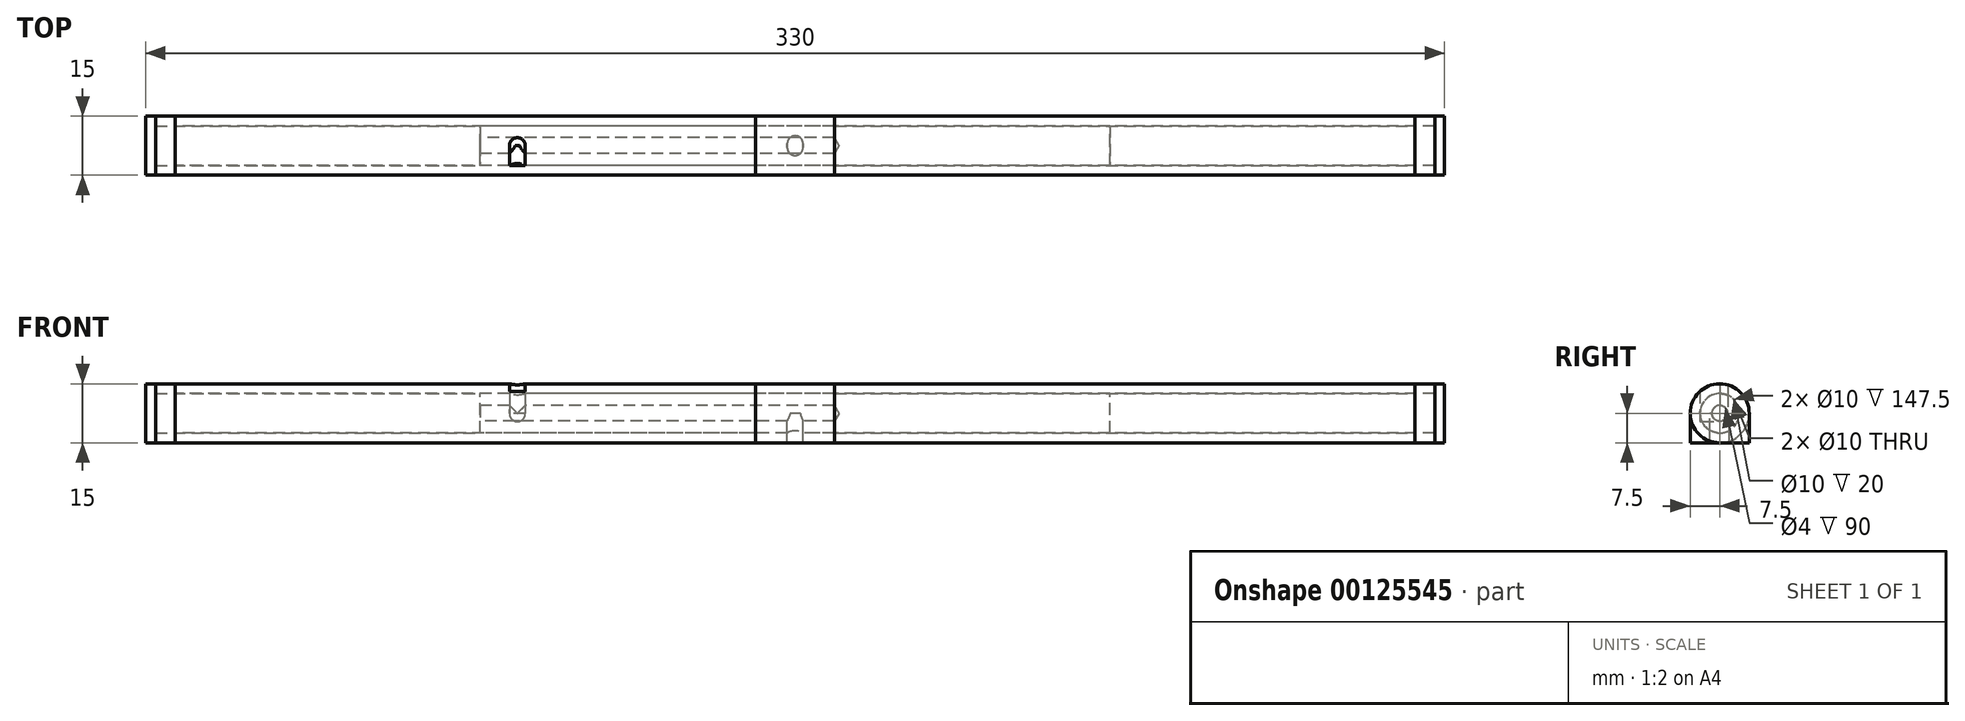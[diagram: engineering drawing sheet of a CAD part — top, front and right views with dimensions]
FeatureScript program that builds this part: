
annotation { "Feature Type Name" : "Feature", "Feature Type Description" : "" }
export const myFeature = defineFeature(function(context is Context, id is Id, definition is map)
    precondition{}
    {
        {
            var Q0;
            Q0=qCreatedBy(makeId("Right.planeOp"),FACE);
            var sketch = newSketch(context, id + "F0", { "sketchPlane" : qUnion([Q0])});
            skCircle(sketch, "E0", {"center": v(0, 0) * mm, "radius": 5 * mm});
            skSolve(sketch);
        }
        {
            var Q0;
            Q0=qCreatedBy(makeId("Right.planeOp"),FACE);
            var sketch = newSketch(context, id + "F1", { "sketchPlane" : qUnion([Q0])});
            skCircle(sketch, "E1", {"center": v(0, 0) * mm, "radius": 7.5 * mm});
            skSolve(sketch);
        }
        {
            var Q0;
            Q0 = qSketchRegion(id + "F1", true);
            extrude(context, id + "F2", {"entities" : qUnion([Q0]), "depth" : 157.5 * mm, "hasSecondDirection" : true, "secondDirectionOppositeDirection" : false, "secondDirectionDepth" : 10 * mm});
        }
        {
            var Q0;
            Q0=makeQuery(id+"F2.opExtrude","CAP_FACE",FACE,{"disambiguationData":[OSD([sQuery(id+"F1.wireOp",EDGE,"E1")])],"isStart":false});
            var sketch = newSketch(context, id + "F3", { "sketchPlane" : qUnion([Q0])});
            skCircle(sketch, "E2", {"center": v(0, 0) * mm, "radius": 5 * mm});
            skSolve(sketch);
        }
        {
            var Q0;
            Q0=sQuery(id+"F3.wireOp",VERTEX,"E2.center");
            var Q1;
            Q1=makeQuery(id+"F2.opExtrude","SWEPT_BODY",BODY,{"disambiguationData":[OSD([sQuery(id+"F1.wireOp",EDGE,"E1")])]});
            hole(context, id + "F4", {"style" : HoleStyle.SIMPLE, "endStyle" : HoleEndStyle.BLIND, "holeDiameter" : 10 * mm, "holeDepth" : 150 * mm, "locations" : qUnion([Q0]), "scope" : qUnion([Q1])});
        }
        {
            var Q0;
            Q0 = qSketchRegion(id + "F0", true);
            extrude(context, id + "F5", {"entities" : qUnion([Q0]), "depth" : 80 * mm, "hasSecondDirection" : true, "secondDirectionOppositeDirection" : true, "secondDirectionDepth" : 80 * mm});
        }
        {
            var Q0;
            Q0=makeQuery(id+"F5.opExtrude","CAP_FACE",FACE,{"disambiguationData":[OSD([sQuery(id+"F0.wireOp",EDGE,"E0")])],"isStart":false});
            extrude(context, id + "F6", {"entities" : qUnion([Q0]), "depth" : 82.5 * mm});
        }
        {
            var Q0;
            Q0 = qSketchRegion(id + "F1", true);
            extrude(context, id + "F7", {"entities" : qUnion([Q0]), "oppositeDirection" : true, "depth" : 157.5 * mm, "hasSecondDirection" : true, "secondDirectionOppositeDirection" : true, "secondDirectionDepth" : 10 * mm});
        }
        {
            var Q0;
            Q0=makeQuery(id+"F7.opExtrude","CAP_FACE",FACE,{"disambiguationData":[OSD([sQuery(id+"F1.wireOp",EDGE,"E1")])],"isStart":false});
            var sketch = newSketch(context, id + "F8", { "sketchPlane" : qUnion([Q0])});
            skCircle(sketch, "E3", {"center": v(0, 0) * mm, "radius": 5 * mm});
            skSolve(sketch);
        }
        {
            var Q0;
            Q0=sQuery(id+"F8.wireOp",VERTEX,"E3.center");
            var Q1;
            Q1=makeQuery(id+"F7.opExtrude","SWEPT_BODY",BODY,{"disambiguationData":[OSD([sQuery(id+"F1.wireOp",EDGE,"E1")])]});
            hole(context, id + "F9", {"style" : HoleStyle.SIMPLE, "endStyle" : HoleEndStyle.BLIND, "holeDiameter" : 10 * mm, "holeDepth" : 157.5 * mm, "locations" : qUnion([Q0]), "scope" : qUnion([Q1])});
        }
        {
            var Q0;
            Q0=makeQuery(id+"F5.opExtrude","CAP_FACE",FACE,{"disambiguationData":[OSD([sQuery(id+"F0.wireOp",EDGE,"E0")])],"isStart":true});
            extrude(context, id + "F10", {"entities" : qUnion([Q0]), "depth" : 82.5 * mm});
        }
        {
            var Q0;
            Q0=makeQuery(id+"F5.opExtrude","CAP_FACE",FACE,{"disambiguationData":[OSD([sQuery(id+"F0.wireOp",EDGE,"E0")])],"isStart":true});
            var sketch = newSketch(context, id + "F11", { "sketchPlane" : qUnion([Q0])});
            skCircle(sketch, "E4", {"center": v(0, 0) * mm, "radius": 2 * mm});
            skSolve(sketch);
        }
        {
            var Q0;
            Q0=sQuery(id+"F11.wireOp",VERTEX,"E4.center");
            var Q1;
            Q1=makeQuery(id+"F5.opExtrude","SWEPT_BODY",BODY,{"disambiguationData":[OSD([sQuery(id+"F0.wireOp",EDGE,"E0")])]});
            hole(context, id + "F12", {"style" : HoleStyle.SIMPLE, "endStyle" : HoleEndStyle.BLIND, "holeDiameter" : 4 * mm, "holeDepth" : 90 * mm, "locations" : qUnion([Q0]), "scope" : qUnion([Q1])});
        }
        {
            var Q0;
            Q0=qCreatedBy(makeId("Top.planeOp"),FACE);
            var sketch = newSketch(context, id + "F13", { "sketchPlane" : qUnion([Q0])});
            skLineSegment(sketch, "E5", {"start": v(-70.56, -0.04) * mm, "end": v(-68.56, -0.04) * mm});
            skLineSegment(sketch, "E6.bottom", {"start": v(-68.56, -0.04) * mm, "end": v(-72.56, -0.04) * mm});
            skLineSegment(sketch, "E7.MirrorCS", {"start": v(-70.56, -0.04) * mm, "end": v(-70.56, 0.46) * mm});
            skArc(sketch, "E8.MirrorCS", {"start": v(-72.56, -0.04) * mm, "mid": v(-70.56, 1.96) * mm, "end": v(-68.56, -0.04) * mm});
            skLineSegment(sketch, "E9.MirrorCS", {"start": v(-68.56, -0.04) * mm, "end": v(-68.56, -5.04) * mm});
            skLineSegment(sketch, "E10.MirrorCS", {"start": v(-72.56, -0.04) * mm, "end": v(-72.56, -5.04) * mm});
            skLineSegment(sketch, "E11.MirrorCS", {"start": v(-70.56, 0.46) * mm, "end": v(-72.5, 0.46) * mm});
            skLineSegment(sketch, "E12.MirrorCS", {"start": v(-68.56, -5.04) * mm, "end": v(-72.56, -5.04) * mm});
            skLineSegment(sketch, "E13.MirrorCS", {"start": v(-70.56, 0.46) * mm, "end": v(-68.62, 0.46) * mm});
            skSolve(sketch);
        }
        {
            var Q0;
            Q0 = qSketchRegion(id + "F13", true);
            extrude(context, id + "F14", {"entities" : qUnion([Q0]), "operationType" : NewBodyOperationType.REMOVE, "depth" : 25 * mm});
        }
        {
            var Q0;
            Q0=qCreatedBy(makeId("Front.planeOp"),FACE);
            var sketch = newSketch(context, id + "F15", { "sketchPlane" : qUnion([Q0])});
            skLineSegment(sketch, "E14", {"start": v(-70.56, 0) * mm, "end": v(-72.56, 0) * mm});
            skLineSegment(sketch, "E15", {"start": v(-72.56, 0) * mm, "end": v(-72.56, -0.1) * mm});
            skLineSegment(sketch, "E16", {"start": v(-72.56, -0.1) * mm, "end": v(-70.56, -0.1) * mm});
            skLineSegment(sketch, "E17", {"start": v(-70.56, -0.1) * mm, "end": v(-68.56, -0.1) * mm});
            skLineSegment(sketch, "E18", {"start": v(-68.56, -0.1) * mm, "end": v(-68.56, 0) * mm});
            skLineSegment(sketch, "E19", {"start": v(-68.56, 0) * mm, "end": v(-68.56, 1) * mm});
            skLineSegment(sketch, "E20", {"start": v(-68.56, 1) * mm, "end": v(-72.56, 1) * mm});
            skLineSegment(sketch, "E21", {"start": v(-72.56, 1) * mm, "end": v(-72.56, 0) * mm});
            skArc(sketch, "E22", {"start": v(-72.56, -0.1) * mm, "mid": v(-70.56, -2.1) * mm, "end": v(-68.56, -0.1) * mm});
            skSolve(sketch);
        }
        {
            var Q0;
            Q0 = qSketchRegion(id + "F15", true);
            extrude(context, id + "F16", {"entities" : qUnion([Q0]), "operationType" : NewBodyOperationType.REMOVE, "depth" : 5 * mm});
        }
        {
            var Q0;
            Q0=qCreatedBy(makeId("Top.planeOp"),FACE);
            var sketch = newSketch(context, id + "F17", { "sketchPlane" : qUnion([Q0])});
            skLineSegment(sketch, "E23.bottom", {"start": v(2, 0.5) * mm, "end": v(-2, 0.5) * mm});
            skLineSegment(sketch, "E23.top", {"start": v(2, -0.5) * mm, "end": v(-2, -0.5) * mm});
            skLineSegment(sketch, "E23.left", {"start": v(2, 0.5) * mm, "end": v(2, -0.5) * mm});
            skLineSegment(sketch, "E23.right", {"start": v(-2, 0.5) * mm, "end": v(-2, -0.5) * mm});
            skPoint(sketch, "E23.middle", {"position": v(0, 0) * mm});
            skArc(sketch, "E24", {"start": v(-2, -0.5) * mm, "mid": v(0, -2.5) * mm, "end": v(2, -0.5) * mm});
            skArc(sketch, "E25", {"start": v(2, 0.5) * mm, "mid": v(0, 2.5) * mm, "end": v(-2, 0.5) * mm});
            skSolve(sketch);
        }
        {
            var Q0;
            Q0 = qSketchRegion(id + "F17", true);
            extrude(context, id + "F18", {"entities" : qUnion([Q0]), "operationType" : NewBodyOperationType.REMOVE, "oppositeDirection" : true, "depth" : 10 * mm});
        }
        {
            var Q0;
            Q0=qCreatedBy(makeId("Top.planeOp"),FACE);
            var sketch = newSketch(context, id + "F19", { "sketchPlane" : qUnion([Q0])});
            skCircle(sketch, "E26", {"center": v(-70.56, 0) * mm, "radius": 2 * mm});
            skSolve(sketch);
        }
        {
            var Q0;
            Q0 = qSketchRegion(id + "F19", true);
            extrude(context, id + "F20", {"entities" : qUnion([Q0]), "operationType" : NewBodyOperationType.REMOVE, "depth" : 10 * mm});
        }
        {
            var Q0;
            Q0=qCreatedBy(makeId("Right.planeOp"),FACE);
            var sketch = newSketch(context, id + "F21", { "sketchPlane" : qUnion([Q0])});
            skCircle(sketch, "E27", {"center": v(0, 0) * mm, "radius": 5 * mm});
            skCircle(sketch, "E28", {"center": v(0, 0) * mm, "radius": 7.5 * mm});
            skLineSegment(sketch, "E29", {"start": v(0, 0) * mm, "end": v(-7.5, 0) * mm});
            skLineSegment(sketch, "E30", {"start": v(0, 0) * mm, "end": v(7.5, 0) * mm});
            skLineSegment(sketch, "E31", {"start": v(0, 0) * mm, "end": v(0, -7.5) * mm});
            skLineSegment(sketch, "E32.bottom", {"start": v(7.5, 0) * mm, "end": v(-7.5, 0) * mm});
            skLineSegment(sketch, "E32.top", {"start": v(7.5, -7.5) * mm, "end": v(-7.5, -7.5) * mm});
            skLineSegment(sketch, "E32.left", {"start": v(7.5, 0) * mm, "end": v(7.5, -7.5) * mm});
            skLineSegment(sketch, "E32.right", {"start": v(-7.5, 0) * mm, "end": v(-7.5, -7.5) * mm});
            skSolve(sketch);
        }
        {
            var Q0;
            Q0 = qSketchRegion(id + "F21", true);
            extrude(context, id + "F22", {"entities" : qUnion([Q0]), "oppositeDirection" : true, "depth" : 162.5 * mm, "hasSecondDirection" : true, "secondDirectionOppositeDirection" : true, "secondDirectionDepth" : 157.5 * mm});
        }
        {
            var Q0;
            Q0 = qSketchRegion(id + "F21", true);
            extrude(context, id + "F23", {"entities" : qUnion([Q0]), "depth" : 162.5 * mm, "hasSecondDirection" : true, "secondDirectionOppositeDirection" : false, "secondDirectionDepth" : 157.5 * mm});
        }
        {
            var Q0;
            Q0 = qSketchRegion(id + "F21", true);
            extrude(context, id + "F24", {"entities" : qUnion([Q0]), "depth" : 10 * mm, "hasSecondDirection" : true, "secondDirectionOppositeDirection" : true, "secondDirectionDepth" : 10 * mm});
        }
        {
            var Q0;
            Q0 = qSketchRegion(id + "F17", true);
            extrude(context, id + "F25", {"entities" : qUnion([Q0]), "operationType" : NewBodyOperationType.REMOVE, "oppositeDirection" : true, "depth" : 25 * mm});
        }
        {
            var Q0;
            Q0=qCreatedBy(makeId("Right.planeOp"),FACE);
            var sketch = newSketch(context, id + "F26", { "sketchPlane" : qUnion([Q0])});
            skLineSegment(sketch, "E33", {"start": v(0, 0) * mm, "end": v(-5, 0) * mm});
            skLineSegment(sketch, "E34", {"start": v(-5, 0) * mm, "end": v(-7.5, 0) * mm});
            skLineSegment(sketch, "E35", {"start": v(0, 0) * mm, "end": v(5, 0) * mm});
            skLineSegment(sketch, "E36", {"start": v(5, 0) * mm, "end": v(7.5, 0) * mm});
            skLineSegment(sketch, "E37", {"start": v(7.5, 0) * mm, "end": v(7.5, -7.5) * mm});
            skLineSegment(sketch, "E38", {"start": v(7.5, -7.5) * mm, "end": v(-7.5, -7.5) * mm});
            skLineSegment(sketch, "E39", {"start": v(-7.5, -7.5) * mm, "end": v(-7.5, 0) * mm});
            skArc(sketch, "E40", {"start": v(7.5, 0) * mm, "mid": v(0, 7.5) * mm, "end": v(-7.5, 0) * mm});
            skSolve(sketch);
        }
        {
            var Q0;
            Q0 = qSketchRegion(id + "F26", true);
            extrude(context, id + "F27", {"entities" : qUnion([Q0]), "depth" : 165 * mm, "hasSecondDirection" : true, "secondDirectionOppositeDirection" : false, "secondDirectionDepth" : 162.5 * mm});
        }
        {
            var Q0;
            Q0 = qSketchRegion(id + "F26", true);
            extrude(context, id + "F28", {"entities" : qUnion([Q0]), "oppositeDirection" : true, "depth" : 165 * mm, "hasSecondDirection" : true, "secondDirectionOppositeDirection" : true, "secondDirectionDepth" : 162.5 * mm});
        }
    });
